# Revit family: RN 12100 Redfil rückspülbar
name_source: partatom
category: Rohrzubehör
units: mm (PartAtom-declared; Revit-internal decimal feet)

## family parameters
Arbeitsebenenbasiert = Nein
Beim Laden mit Abzugskörper schneiden = Nein
Bemaßung runder Anschluss = Durchmesser verwenden
Gemeinsam genutzt = Nein
Immer vertikal = Ja
Teiletyp = Ventil - Zerlegung in

## types (4) — shared parameters
1.010.00.2 Blattnummer der Richtlinie = 17
1.010.00.3 Ausgabedatum (Monat) der Richtlinie = 201601
1.010.00.4 Herstellername = R. Nussbaum AG
1.010.00.5 Revisionsdatum der Datei = 20190528
1.010.00.6 Webadresse des Herstellers = http://www.nussbaum.ch
1.100.00.3 Sortiernummer für Anzeigereihenfolge = 9
1.100.00.4 Produktbezeichnung = Filterkombination, Filter und Schmutzfänger
1.960/3L.00.8 Link (URL) = https://www.nussbaum.ch
17.700.00.4 Armaturentyp = 8
17.700.00.7 Maximale Betriebstemperatur TB [°C] = 30
17.700.00.8 Maximaler Betriebsdruck (Arbeitsdruck) ps [1.0 · 105 Pa] = 16
Connector Visibility = Nein
EnclosingSpace Visibility = Nein
Hersteller = R. Nussbauzm AG
URL = https://www.nussbaum.ch

## per-type parameters (varying)
- DN 25: 1.800.00.3 TGA-Nummer=00900200000000000000000000001300700000000000000001???00000; 1.810.00.3 Hersteller-Bestellnummer=12100.36; 1.810.00.4 DATANORM-Nummer=12100.36; 1.810.00.5 StLB-Nummer=613.315; 1.810.00.6 GTIN-Nummer=7612945700209; 17.700.00.30 Produktbeschreibung=12100.36, Redfil rückspülbar, ohne Anschlussverschraubungen, DN=25; 17.700.00.5 Nennweite DN=25; 17.700.00.6 kvs-Wert [m3/h]=6; CONNECTOR0_DIAMETER_dX_0r=25 mm  [stored 0.082021 ft]; CONNECTOR0_dX_00=50 mm; CONNECTOR0_dX_01=38 mm; CONNECTOR0_ref_dX=50 mm; CONNECTOR0_ref_dY=93 mm; CONNECTOR0_ref_dZ=339 mm  [stored 1.1122 ft]; CONNECTOR1_DIAMETER_dX_0r=25 mm  [stored 0.082021 ft]; CONNECTOR1_dX_00=38 mm; CONNECTOR1_dX_01=50 mm; CONNECTOR1_ref_dX=50 mm; CONNECTOR1_ref_dY=93 mm; CONNECTOR1_ref_dZ=339 mm  [stored 1.1122 ft]; Modell=12100.36; R. Nussbaum AG 12100.36 de Visibility=Ja; R. Nussbaum AG 12100.37 de Visibility=Nein; R. Nussbaum AG 12100.38 de Visibility=Nein; R. Nussbaum AG 12100.39 de Visibility=Nein; Typenkommentare=Redfil rückspülbarDN 25
- DN 32: 1.800.00.3 TGA-Nummer=00900200000000000000000000001300700000000000000002???00000; 1.810.00.3 Hersteller-Bestellnummer=12100.37; 1.810.00.4 DATANORM-Nummer=12100.37; 1.810.00.5 StLB-Nummer=613.316; 1.810.00.6 GTIN-Nummer=7612945700216; 17.700.00.30 Produktbeschreibung=12100.37, Redfil rückspülbar, ohne Anschlussverschraubungen, DN=32; 17.700.00.5 Nennweite DN=32; 17.700.00.6 kvs-Wert [m3/h]=7.2; CONNECTOR0_DIAMETER_dX_0r=32 mm  [stored 0.104987 ft]; CONNECTOR0_dX_00=60 mm; CONNECTOR0_dX_01=46 mm; CONNECTOR0_ref_dX=60 mm; CONNECTOR0_ref_dY=96 mm  [stored 0.314961 ft]; CONNECTOR0_ref_dZ=339 mm  [stored 1.1122 ft]; CONNECTOR1_DIAMETER_dX_0r=32 mm  [stored 0.104987 ft]; CONNECTOR1_dX_00=46 mm; CONNECTOR1_dX_01=60 mm; CONNECTOR1_ref_dX=60 mm; CONNECTOR1_ref_dY=100 mm  [stored 0.328084 ft]; CONNECTOR1_ref_dZ=339 mm  [stored 1.1122 ft]; Modell=12100.37; R. Nussbaum AG 12100.36 de Visibility=Nein; R. Nussbaum AG 12100.37 de Visibility=Ja; R. Nussbaum AG 12100.38 de Visibility=Nein; R. Nussbaum AG 12100.39 de Visibility=Nein; Typenkommentare=Redfil rückspülbarDN 32
- DN 40: 1.800.00.3 TGA-Nummer=00900200000000000000000000001300700000000000000003???00000; 1.810.00.3 Hersteller-Bestellnummer=12100.38; 1.810.00.4 DATANORM-Nummer=12100.38; 1.810.00.5 StLB-Nummer=613.317; 1.810.00.6 GTIN-Nummer=7612945703156; 17.700.00.30 Produktbeschreibung=12100.38, Redfil rückspülbar, ohne Anschlussverschraubungen, DN=40; 17.700.00.5 Nennweite DN=40; 17.700.00.6 kvs-Wert [m3/h]=12; CONNECTOR0_DIAMETER_dX_0r=40 mm; CONNECTOR0_dX_00=73 mm; CONNECTOR0_dX_01=60 mm; CONNECTOR0_ref_dX=73 mm; CONNECTOR0_ref_dY=135 mm; CONNECTOR0_ref_dZ=385 mm; CONNECTOR1_DIAMETER_dX_0r=40 mm; CONNECTOR1_dX_00=60 mm; CONNECTOR1_dX_01=73 mm; CONNECTOR1_ref_dX=73 mm; CONNECTOR1_ref_dY=135 mm; CONNECTOR1_ref_dZ=430 mm; Modell=12100.38; R. Nussbaum AG 12100.36 de Visibility=Nein; R. Nussbaum AG 12100.37 de Visibility=Nein; R. Nussbaum AG 12100.38 de Visibility=Ja; R. Nussbaum AG 12100.39 de Visibility=Nein; Typenkommentare=Redfil rückspülbarDN 40
- DN 50: 1.800.00.3 TGA-Nummer=00900200000000000000000000001300700000000000000004???00000; 1.810.00.3 Hersteller-Bestellnummer=12100.39; 1.810.00.4 DATANORM-Nummer=12100.39; 1.810.00.5 StLB-Nummer=613.318; 1.810.00.6 GTIN-Nummer=7612945703163; 17.700.00.30 Produktbeschreibung=12100.39, Redfil rückspülbar, ohne Anschlussverschraubungen, DN=50; 17.700.00.5 Nennweite DN=50; 17.700.00.6 kvs-Wert [m3/h]=13.2; CONNECTOR0_DIAMETER_dX_0r=50 mm; CONNECTOR0_dX_00=89 mm; CONNECTOR0_dX_01=69 mm; CONNECTOR0_ref_dX=89 mm; CONNECTOR0_ref_dY=135 mm; CONNECTOR0_ref_dZ=385 mm; CONNECTOR1_DIAMETER_dX_0r=50 mm; CONNECTOR1_dX_00=73 mm; CONNECTOR1_dX_01=86 mm; CONNECTOR1_ref_dX=86 mm; CONNECTOR1_ref_dY=135 mm; CONNECTOR1_ref_dZ=385 mm; Modell=12100.39; R. Nussbaum AG 12100.36 de Visibility=Nein; R. Nussbaum AG 12100.37 de Visibility=Nein; R. Nussbaum AG 12100.38 de Visibility=Nein; R. Nussbaum AG 12100.39 de Visibility=Ja; Typenkommentare=Redfil rückspülbarDN 50

note: [stored X ft] marks values corroborated as IEEE doubles in the binary element streams (Revit-internal decimal feet)

## geometry (parser evidence)
native form markers: Sweep x1
no freeform markers — native parametric forms only
